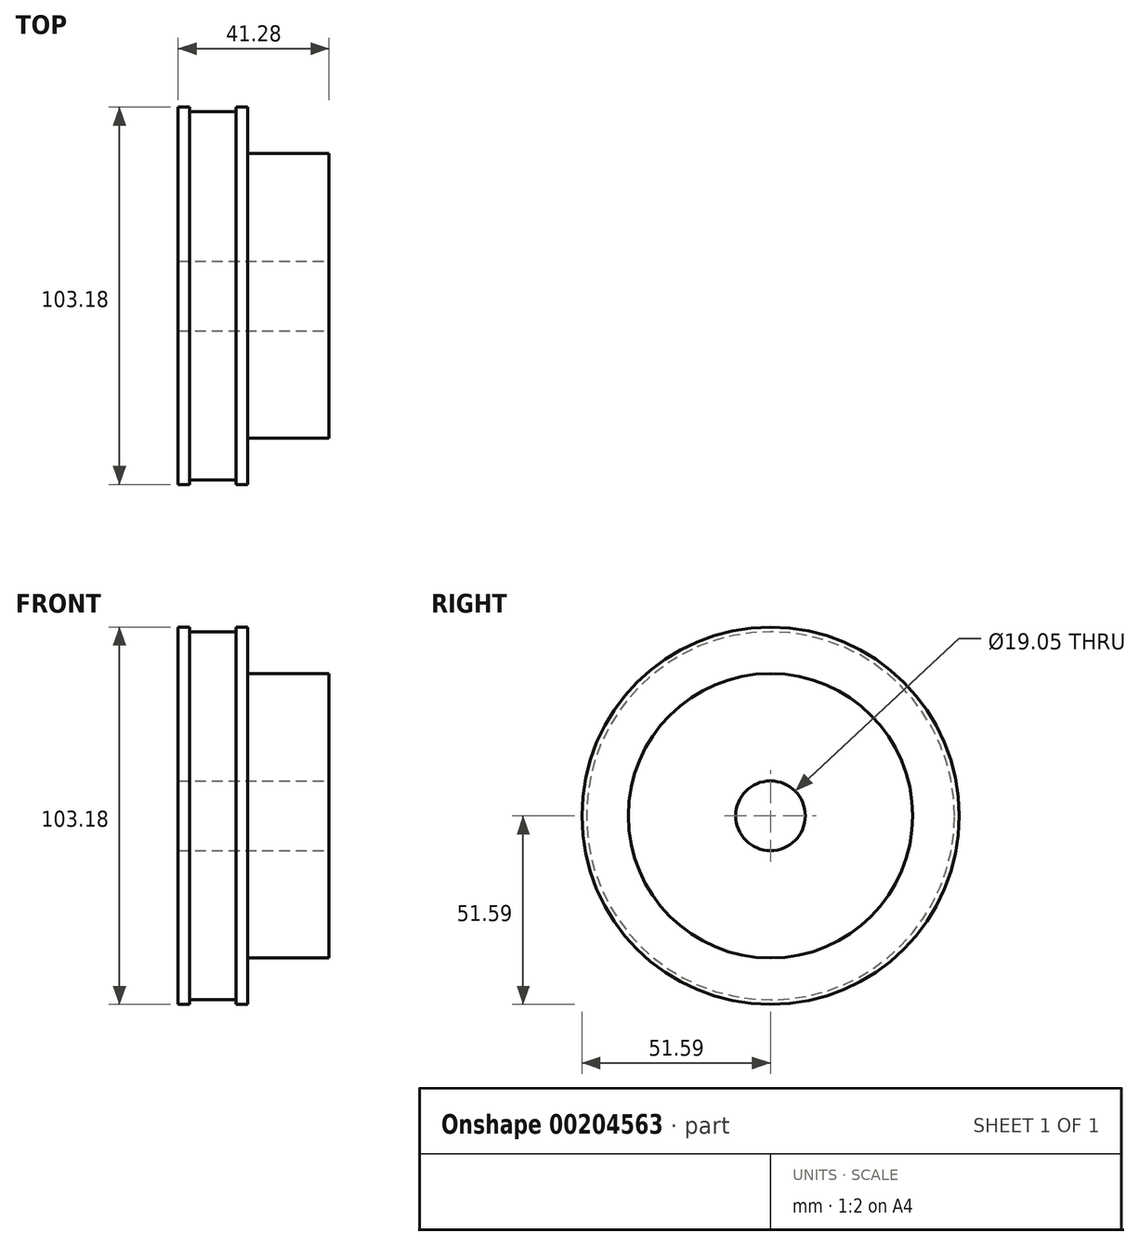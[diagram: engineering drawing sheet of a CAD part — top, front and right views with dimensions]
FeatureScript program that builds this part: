
annotation { "Feature Type Name" : "Feature", "Feature Type Description" : "" }
export const myFeature = defineFeature(function(context is Context, id is Id, definition is map)
    precondition{}
    {
        {
            var Q0;
            Q0=qCreatedBy(makeId("Right.planeOp"),FACE);
            var sketch = newSketch(context, id + "F0", { "sketchPlane" : qUnion([Q0])});
            skCircle(sketch, "E0", {"center": v(0, 0) * mm, "radius": 51.6 * mm});
            skSolve(sketch);
        }
        {
            var Q0;
            Q0 = qSketchRegion(id + "F0", true);
            extrude(context, id + "F1", {"entities" : qUnion([Q0]), "endBound" : BoundingType.SYMMETRIC, "depth" : 19.05 * mm});
        }
        {
            var Q0;
            Q0=makeQuery(id+"F1.opExtrude","CAP_FACE",FACE,{"disambiguationData":[OSD([sQuery(id+"F0.wireOp",EDGE,"E0")])],"isStart":false});
            var sketch = newSketch(context, id + "F2", { "sketchPlane" : qUnion([Q0])});
            skCircle(sketch, "E1", {"center": v(0, 0) * mm, "radius": 38.9 * mm});
            skSolve(sketch);
        }
        {
            var Q0;
            Q0 = qSketchRegion(id + "F2", true);
            extrude(context, id + "F3", {"entities" : qUnion([Q0]), "operationType" : NewBodyOperationType.ADD, "depth" : 22.22 * mm});
        }
        {
            var Q0;
            Q0=qCreatedBy(makeId("Front.planeOp"),FACE);
            var sketch = newSketch(context, id + "F4", { "sketchPlane" : qUnion([Q0])});
            skLineSegment(sketch, "E2", {"start": v(-9.52, 51.6) * mm, "end": v(9.53, 51.6) * mm, "construction": true});
            skLineSegment(sketch, "E3", {"start": v(-54.27, 0) * mm, "end": v(58.03, 0) * mm, "construction": true});
            skLineSegment(sketch, "E4", {"start": v(0, 80.11) * mm, "end": v(0, 38.86) * mm, "construction": true});
            skLineSegment(sketch, "E5.bottom", {"start": v(-6.35, 50.32) * mm, "end": v(6.35, 50.32) * mm});
            skLineSegment(sketch, "E5.top", {"start": v(-6.35, 52.86) * mm, "end": v(6.35, 52.86) * mm});
            skLineSegment(sketch, "E5.left", {"start": v(-6.35, 50.32) * mm, "end": v(-6.35, 52.86) * mm});
            skLineSegment(sketch, "E5.right", {"start": v(6.35, 50.32) * mm, "end": v(6.35, 52.86) * mm});
            skPoint(sketch, "E5.middle", {"position": v(0, 51.6) * mm});
            skSolve(sketch);
        }
        {
            var Q0;
            Q0=makeQuery(id+"F4.imprint","IMPRINT",FACE,{"disambiguationData":[TD([[makeQuery(id+"F4.imprint","IMPRINT",EDGE,{"derivedFrom":sQuery(id+"F4.wireOp",EDGE,"E5.bottom")}),1.0]])]});
            var Q1;
            Q1=sQuery(id+"F4.wireOp",EDGE,"E3");
            revolve(context, id + "F5", {"operationType" : NewBodyOperationType.REMOVE, "entities" : qUnion([Q0]), "axis" : qUnion([Q1]), "revolveType" : RevolveType.FULL, "oppositeDirection" : true});
        }
        {
            var Q0;
            Q0=makeQuery(id+"F3.opExtrude","CAP_FACE",FACE,{"disambiguationData":[OSD([sQuery(id+"F2.wireOp",EDGE,"E1")])],"isStart":false});
            var sketch = newSketch(context, id + "F6", { "sketchPlane" : qUnion([Q0])});
            skPoint(sketch, "E6", {"position": v(0, 0) * mm});
            skSolve(sketch);
        }
        {
            var Q0;
            Q0=sQuery(id+"F6.wireOp",VERTEX,"E6");
            var Q1;
            Q1=makeQuery(id+"F1.opExtrude","SWEPT_BODY",BODY,{"disambiguationData":[OSD([sQuery(id+"F0.wireOp",EDGE,"E0")])]});
            hole(context, id + "F7", {"style" : HoleStyle.SIMPLE, "endStyle" : HoleEndStyle.THROUGH, "holeDiameter" : 19.05 * mm, "locations" : qUnion([Q0]), "scope" : qUnion([Q1]), "isTappedThrough" : true});
        }
    });
